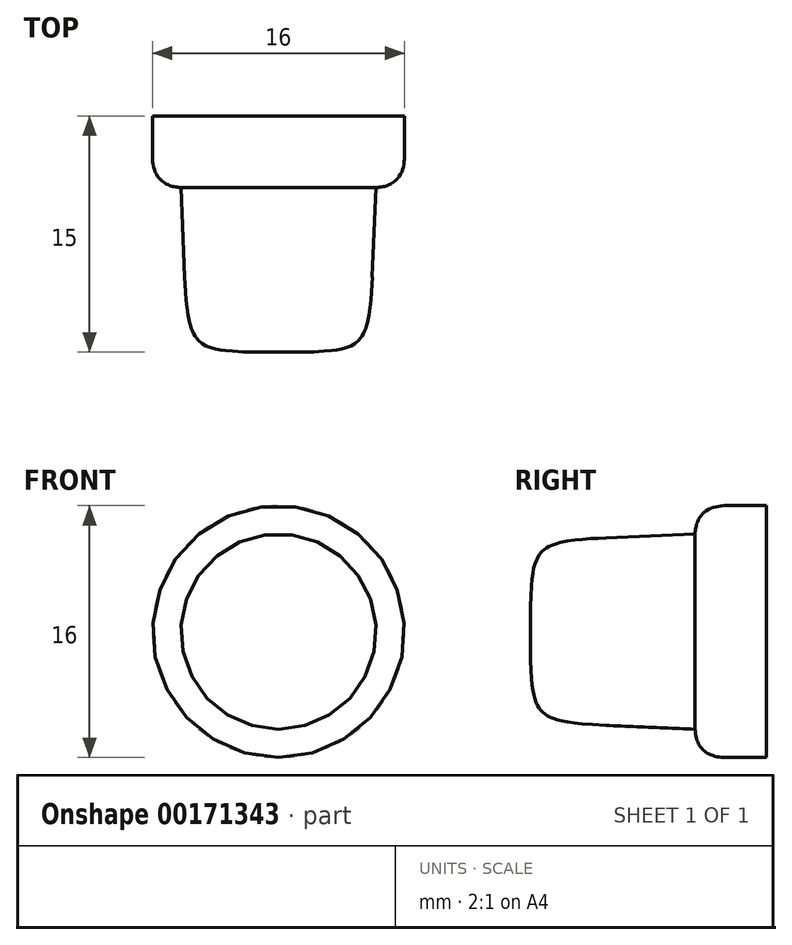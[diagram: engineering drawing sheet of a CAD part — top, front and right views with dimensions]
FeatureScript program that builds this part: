
annotation { "Feature Type Name" : "Feature", "Feature Type Description" : "" }
export const myFeature = defineFeature(function(context is Context, id is Id, definition is map)
    precondition{}
    {
        {
            var Q0;
            Q0=qCreatedBy(makeId("Front.planeOp"),FACE);
            var sketch = newSketch(context, id + "F0", { "sketchPlane" : qUnion([Q0])});
            skCircle(sketch, "E0", {"center": v(0, 0) * mm, "radius": 8 * mm});
            skCircle(sketch, "E1", {"center": v(0, 0) * mm, "radius": 6.4 * mm});
            skSolve(sketch);
        }
        {
            var Q0;
            Q0=makeQuery(id+"F0.imprint","IMPRINT",FACE,{"disambiguationData":[TD([[makeQuery(id+"F0.imprint","IMPRINT",EDGE,{"derivedFrom":sQuery(id+"F0.wireOp",EDGE,"E0")}),1.0]])]});
            var Q1;
            Q1=makeQuery(id+"F0.imprint","IMPRINT",FACE,{"disambiguationData":[TD([[makeQuery(id+"F0.imprint","IMPRINT",EDGE,{"derivedFrom":sQuery(id+"F0.wireOp",EDGE,"E1")}),1.0]])]});
            extrude(context, id + "F1", {"entities" : qUnion([Q0, Q1]), "depth" : 4.55 * mm});
        }
        {
            var Q0;
            Q0=makeQuery(id+"F1.opExtrude","CAP_FACE",FACE,{"disambiguationData":[OSD([sQuery(id+"F0.wireOp",EDGE,"E0")])],"isStart":false});
            fillet(context, id + "F2", {"entities" : qUnion([Q0]), "radius" : 2 * mm, "rho" : 0.5, "crossSection" : FilletCrossSection.CONIC, "allowEdgeOverflow" : false});
        }
        {
            var Q0;
            Q0=qCreatedBy(makeId("Top.planeOp"),FACE);
            var sketch = newSketch(context, id + "F3", { "sketchPlane" : qUnion([Q0])});
            skLineSegment(sketch, "E2", {"start": v(0, 0) * mm, "end": v(-6.4, 0) * mm});
            skLineSegment(sketch, "E3", {"start": v(-6.4, 0) * mm, "end": v(-5.75, -15) * mm});
            skLineSegment(sketch, "E4", {"start": v(-5.75, -15) * mm, "end": v(0, -15) * mm});
            skLineSegment(sketch, "E5", {"start": v(0, -15) * mm, "end": v(0, 0) * mm});
            skSolve(sketch);
        }
        {
            var Q0;
            Q0=makeQuery(id+"F3.imprint","IMPRINT",FACE,{"disambiguationData":[TD([[makeQuery(id+"F3.imprint","IMPRINT",EDGE,{"derivedFrom":sQuery(id+"F3.wireOp",EDGE,"E2")}),1.0]])]});
            var Q1;
            Q1=sQuery(id+"F3.wireOp",EDGE,"E5");
            revolve(context, id + "F4", {"operationType" : NewBodyOperationType.ADD, "entities" : qUnion([Q0]), "axis" : qUnion([Q1]), "revolveType" : RevolveType.FULL});
        }
        {
            var Q0;
            Q0=makeQuery(id+"F4.opRevolve","SWEPT_EDGE",EDGE,{"disambiguationData":[OSD([sQuery(id+"F3.wireOp",EDGE,"E3"),sQuery(id+"F3.wireOp",EDGE,"E4")])]});
            fillet(context, id + "F5", {"entities" : qUnion([Q0]), "radius" : 5 * mm, "tangentPropagation" : true, "rho" : .7, "crossSection" : FilletCrossSection.CONIC, "allowEdgeOverflow" : false});
        }
    });
